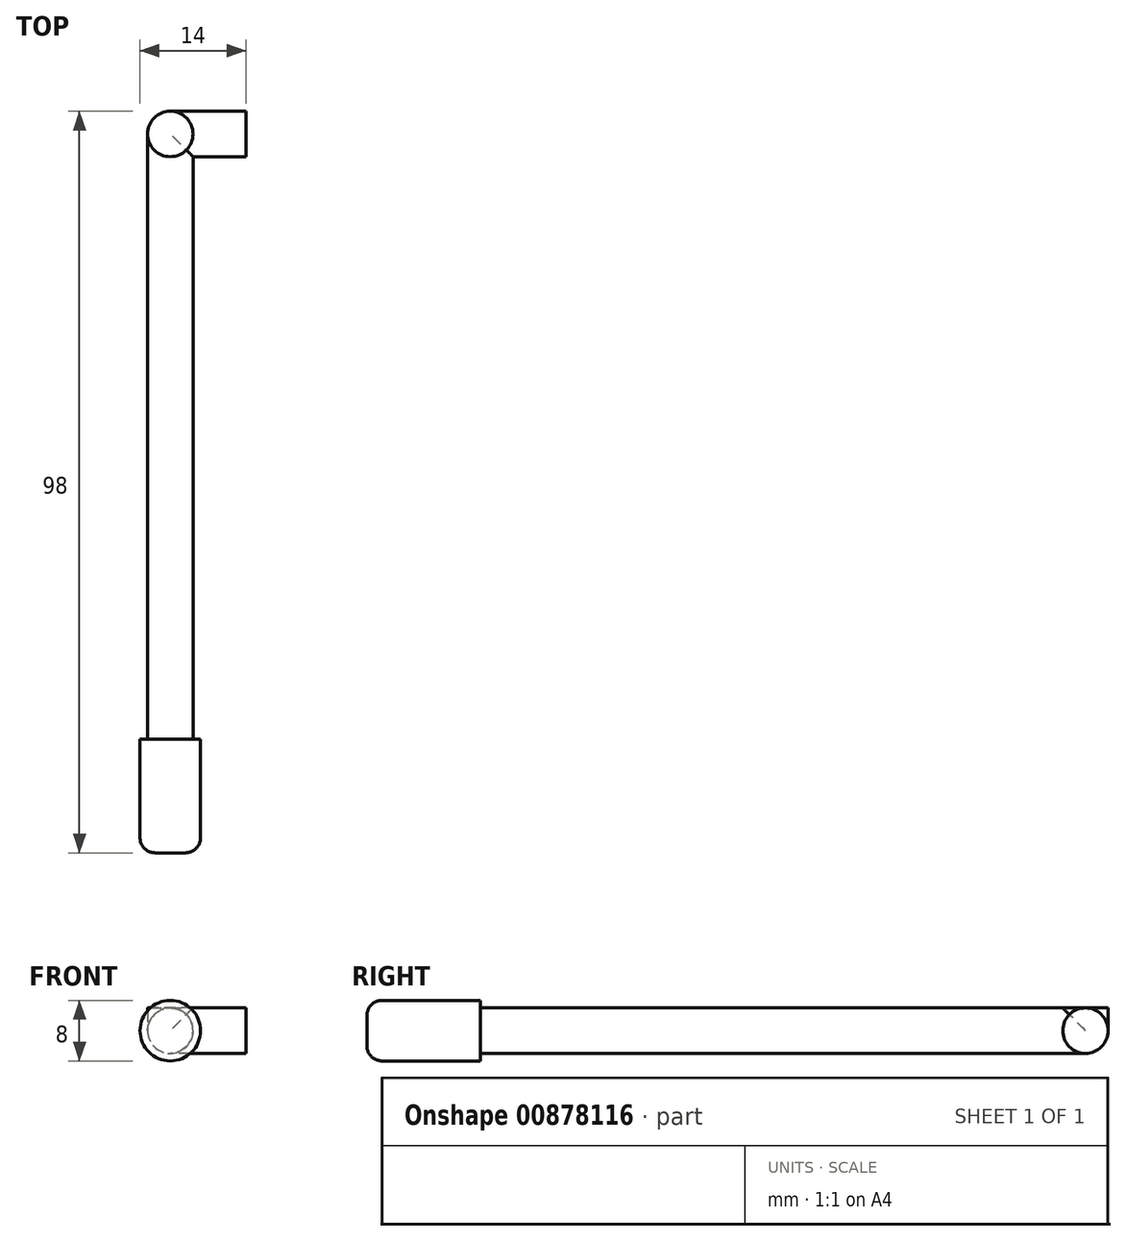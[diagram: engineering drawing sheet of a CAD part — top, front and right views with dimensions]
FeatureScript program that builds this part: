
annotation { "Feature Type Name" : "Feature", "Feature Type Description" : "" }
export const myFeature = defineFeature(function(context is Context, id is Id, definition is map)
    precondition{}
    {
        {
            var Q0;
            Q0=qCreatedBy(makeId("Front.planeOp"),FACE);
            var sketch = newSketch(context, id + "F0", { "sketchPlane" : qUnion([Q0])});
            skCircle(sketch, "E0", {"center": v(0, 0) * mm, "radius": 3 * mm});
            skSolve(sketch);
        }
        {
            var Q0;
            Q0=makeQuery(id+"F0.imprint","IMPRINT",FACE,{"disambiguationData":[TD([[makeQuery(id+"F0.imprint","IMPRINT",EDGE,{"derivedFrom":sQuery(id+"F0.wireOp",EDGE,"E0")}),1.0]])]});
            extrude(context, id + "F1", {"entities" : qUnion([Q0]), "depth" : 80 * mm, "offsetDistance" : 25 * mm});
        }
        {
            var Q0;
            Q0=makeQuery(id+"F1.opExtrude","CAP_FACE",FACE,{"disambiguationData":[OSD([sQuery(id+"F0.wireOp",EDGE,"E0")])],"isStart":false});
            var sketch = newSketch(context, id + "F2", { "sketchPlane" : qUnion([Q0])});
            skCircle(sketch, "E1", {"center": v(0, 0) * mm, "radius": 4 * mm});
            skSolve(sketch);
        }
        {
            var Q0;
            Q0=makeQuery(id+"F2.imprint","IMPRINT",FACE,{"disambiguationData":[TD([[makeQuery(id+"F2.imprint","IMPRINT",EDGE,{"derivedFrom":makeQuery(id+"F1.opExtrude","CAP_EDGE",EDGE,{"disambiguationData":[OSD([sQuery(id+"F0.wireOp",EDGE,"E0")])],"isStart":false})}),1.0]])]});
            var Q1;
            Q1=makeQuery(id+"F2.imprint","IMPRINT",FACE,{"disambiguationData":[TD([[makeQuery(id+"F2.imprint","IMPRINT",EDGE,{"derivedFrom":sQuery(id+"F2.wireOp",EDGE,"E1")}),1.0]])]});
            extrude(context, id + "F3", {"entities" : qUnion([Q0, Q1]), "operationType" : NewBodyOperationType.ADD, "depth" : 15 * mm, "offsetDistance" : 25 * mm});
        }
        {
            var Q0;
            Q0=makeQuery(id+"F3.opExtrude","CAP_FACE",FACE,{"disambiguationData":[OSD([sQuery(id+"F2.wireOp",EDGE,"E1")])],"isStart":false});
            fillet(context, id + "F4", {"entities" : qUnion([Q0]), "radius" : 2 * mm, "tangentPropagation" : true, "allowEdgeOverflow" : false});
        }
        {
            var Q0;
            Q0=qCreatedBy(makeId("Right.planeOp"),FACE);
            var sketch = newSketch(context, id + "F5", { "sketchPlane" : qUnion([Q0])});
            skCircle(sketch, "E2", {"center": v(0, 0) * mm, "radius": 3 * mm});
            skSolve(sketch);
        }
        {
            var Q0;
            Q0=makeQuery(id+"F5.imprint","IMPRINT",FACE,{"disambiguationData":[TD([[makeQuery(id+"F5.imprint","IMPRINT",EDGE,{"derivedFrom":sQuery(id+"F5.wireOp",EDGE,"E2")}),1.0]])]});
            extrude(context, id + "F6", {"entities" : qUnion([Q0]), "operationType" : NewBodyOperationType.ADD, "depth" : 10 * mm, "offsetDistance" : 25 * mm});
        }
        {
            var Q0;
            Q0=qCreatedBy(makeId("Top.planeOp"),FACE);
            var sketch = newSketch(context, id + "F7", { "sketchPlane" : qUnion([Q0])});
            skCircle(sketch, "E3", {"center": v(0, 0) * mm, "radius": 3 * mm});
            skSolve(sketch);
        }
        {
            var Q0;
            Q0 = qSketchRegion(id + "F7", true);
            extrude(context, id + "F8", {"entities" : qUnion([Q0]), "operationType" : NewBodyOperationType.ADD, "depth" : 3 * mm, "offsetDistance" : 25 * mm});
        }
        {
            var Q0;
            Q0=makeQuery(id+"F8.opExtrude","CAP_FACE",FACE,{"disambiguationData":[OSD([sQuery(id+"F7.wireOp",EDGE,"E3")])],"isStart":true});
            extrude(context, id + "F9", {"entities" : qUnion([Q0]), "operationType" : NewBodyOperationType.ADD, "depth" : 3 * mm, "offsetDistance" : 25 * mm});
        }
        {
            var Q0;
            Q0=makeQuery(id+"F9.opExtrude","CAP_EDGE",EDGE,{"disambiguationData":[OSD([sQuery(id+"F7.wireOp",EDGE,"E3")])],"isStart":false});
            fillet(context, id + "F10", {"entities" : qUnion([Q0]), "radius" : 3 * mm, "tangentPropagation" : true, "allowEdgeOverflow" : false});
        }
    });
